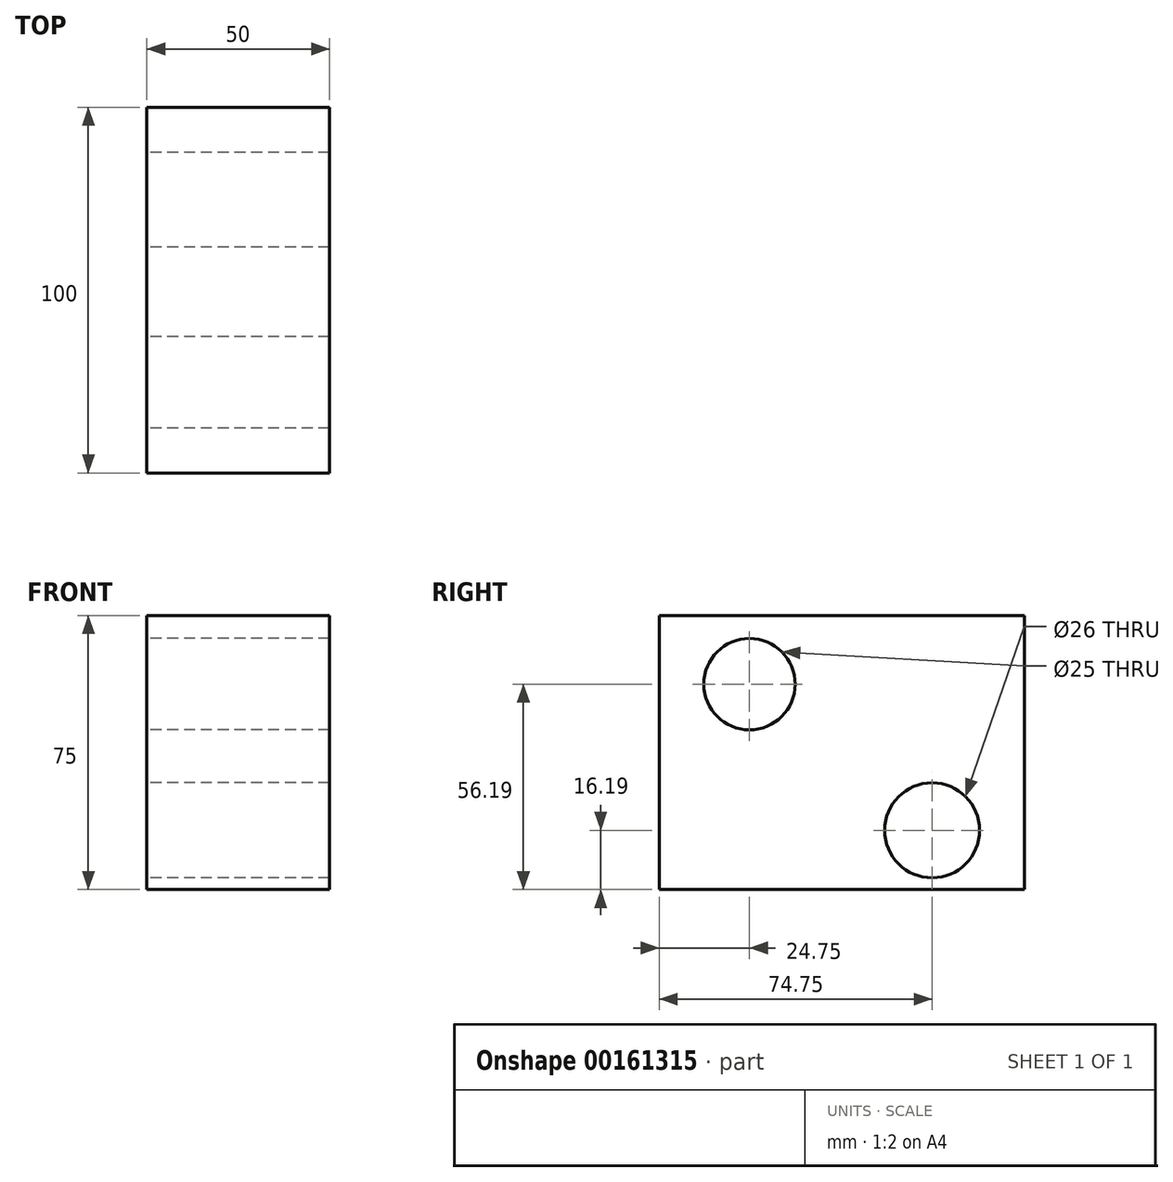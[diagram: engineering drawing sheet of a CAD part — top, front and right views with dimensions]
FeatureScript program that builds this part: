
annotation { "Feature Type Name" : "Feature", "Feature Type Description" : "" }
export const myFeature = defineFeature(function(context is Context, id is Id, definition is map)
    precondition{}
    {
        {
            var Q0;
            Q0=qCreatedBy(makeId("Right.planeOp"),FACE);
            var sketch = newSketch(context, id + "F0", { "sketchPlane" : qUnion([Q0])});
            skLineSegment(sketch, "E0.bottom", {"start": v(-49.75, 38.81) * mm, "end": v(50.25, 38.81) * mm});
            skLineSegment(sketch, "E0.top", {"start": v(-49.75, -36.19) * mm, "end": v(50.25, -36.19) * mm});
            skLineSegment(sketch, "E0.left", {"start": v(-49.75, 38.81) * mm, "end": v(-49.75, -36.19) * mm});
            skLineSegment(sketch, "E0.right", {"start": v(50.25, 38.81) * mm, "end": v(50.25, -36.19) * mm});
            skSolve(sketch);
        }
        {
            var Q0;
            Q0 = qSketchRegion(id + "F0", true);
            extrude(context, id + "F1", {"entities" : qUnion([Q0]), "endBound" : BoundingType.SYMMETRIC, "depth" : 50 * mm});
        }
        {
            var Q0;
            Q0=qCreatedBy(makeId("Right.planeOp"),FACE);
            var sketch = newSketch(context, id + "F2", { "sketchPlane" : qUnion([Q0])});
            skCircle(sketch, "E1", {"center": v(-25, 20) * mm, "radius": 12.5 * mm});
            skCircle(sketch, "E2", {"center": v(25, -20) * mm, "radius": 13 * mm});
            skSolve(sketch);
        }
        {
            var Q0;
            Q0 = qSketchRegion(id + "F2", true);
            extrude(context, id + "F3", {"entities" : qUnion([Q0]), "operationType" : NewBodyOperationType.REMOVE, "endBound" : BoundingType.SYMMETRIC, "depth" : 100 * mm});
        }
    });
